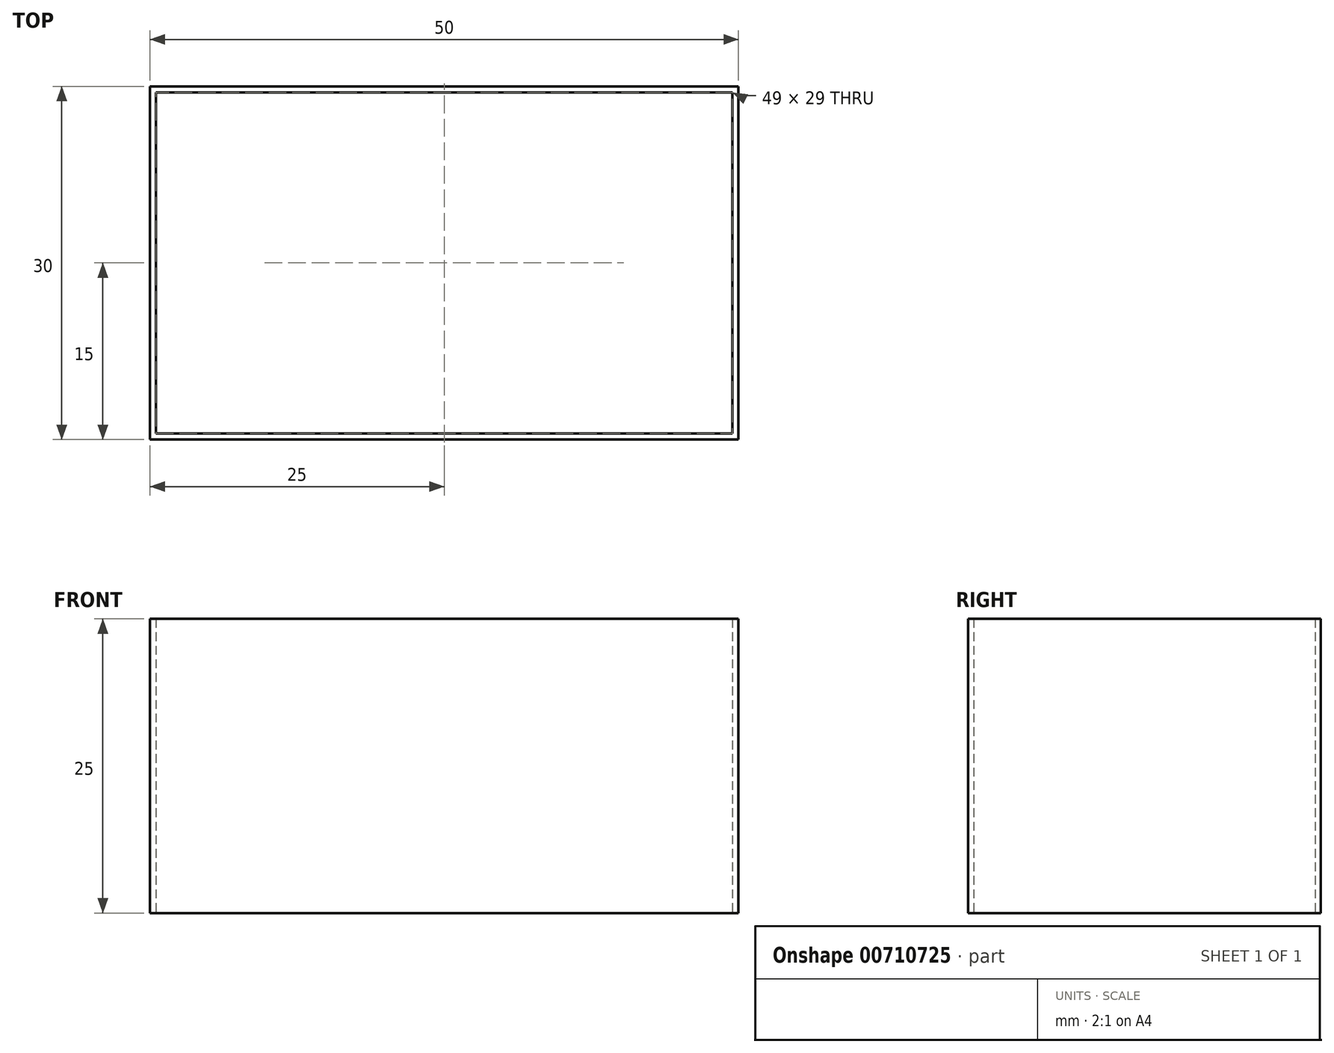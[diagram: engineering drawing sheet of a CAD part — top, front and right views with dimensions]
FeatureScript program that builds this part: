
annotation { "Feature Type Name" : "Feature", "Feature Type Description" : "" }
export const myFeature = defineFeature(function(context is Context, id is Id, definition is map)
    precondition{}
    {
        {
            var Q0;
            Q0=qCreatedBy(makeId("Top.planeOp"),FACE);
            var sketch = newSketch(context, id + "F0", { "sketchPlane" : qUnion([Q0])});
            skLineSegment(sketch, "E0.bottom", {"start": v(25, -15) * mm, "end": v(-25, -15) * mm});
            skLineSegment(sketch, "E0.top", {"start": v(25, 15) * mm, "end": v(-25, 15) * mm});
            skLineSegment(sketch, "E0.left", {"start": v(25, -15) * mm, "end": v(25, 15) * mm});
            skLineSegment(sketch, "E0.right", {"start": v(-25, -15) * mm, "end": v(-25, 15) * mm});
            skPoint(sketch, "E0.middle", {"position": v(0, 0) * mm});
            skSolve(sketch);
        }
        {
            var Q0;
            Q0=makeQuery(id+"F0.imprint","IMPRINT",FACE,{"disambiguationData":[TD([[makeQuery(id+"F0.imprint","IMPRINT",EDGE,{"derivedFrom":sQuery(id+"F0.wireOp",EDGE,"E0.bottom")}),-1.0]])]});
            extrude(context, id + "F1", {"entities" : qUnion([Q0]), "depth" : 25 * mm, "offsetDistance" : 25 * mm});
        }
        {
            var Q0;
            Q0=qCreatedBy(makeId("Top.planeOp"),FACE);
            var sketch = newSketch(context, id + "F2", { "sketchPlane" : qUnion([Q0])});
            skLineSegment(sketch, "E1.bottom", {"start": v(24.5, -14.5) * mm, "end": v(-24.5, -14.5) * mm});
            skLineSegment(sketch, "E1.top", {"start": v(24.5, 14.5) * mm, "end": v(-24.5, 14.5) * mm});
            skLineSegment(sketch, "E1.left", {"start": v(24.5, -14.5) * mm, "end": v(24.5, 14.5) * mm});
            skLineSegment(sketch, "E1.right", {"start": v(-24.5, -14.5) * mm, "end": v(-24.5, 14.5) * mm});
            skPoint(sketch, "E1.middle", {"position": v(0, 0) * mm});
            skSolve(sketch);
        }
        {
            var Q0;
            Q0 = qSketchRegion(id + "F2", true);
            var Q1;
            Q1=makeQuery(id+"F1.opExtrude","CAP_FACE",FACE,{"disambiguationData":[OSD([sQuery(id+"F0.wireOp",EDGE,"E0.bottom"),sQuery(id+"F0.wireOp",EDGE,"E0.top"),sQuery(id+"F0.wireOp",EDGE,"E0.left"),sQuery(id+"F0.wireOp",EDGE,"E0.right")])],"isStart":false});
            extrude(context, id + "F3", {"entities" : qUnion([Q0, Q1]), "operationType" : NewBodyOperationType.REMOVE, "depth" : 25 * mm, "offsetDistance" : 25 * mm});
        }
    });
